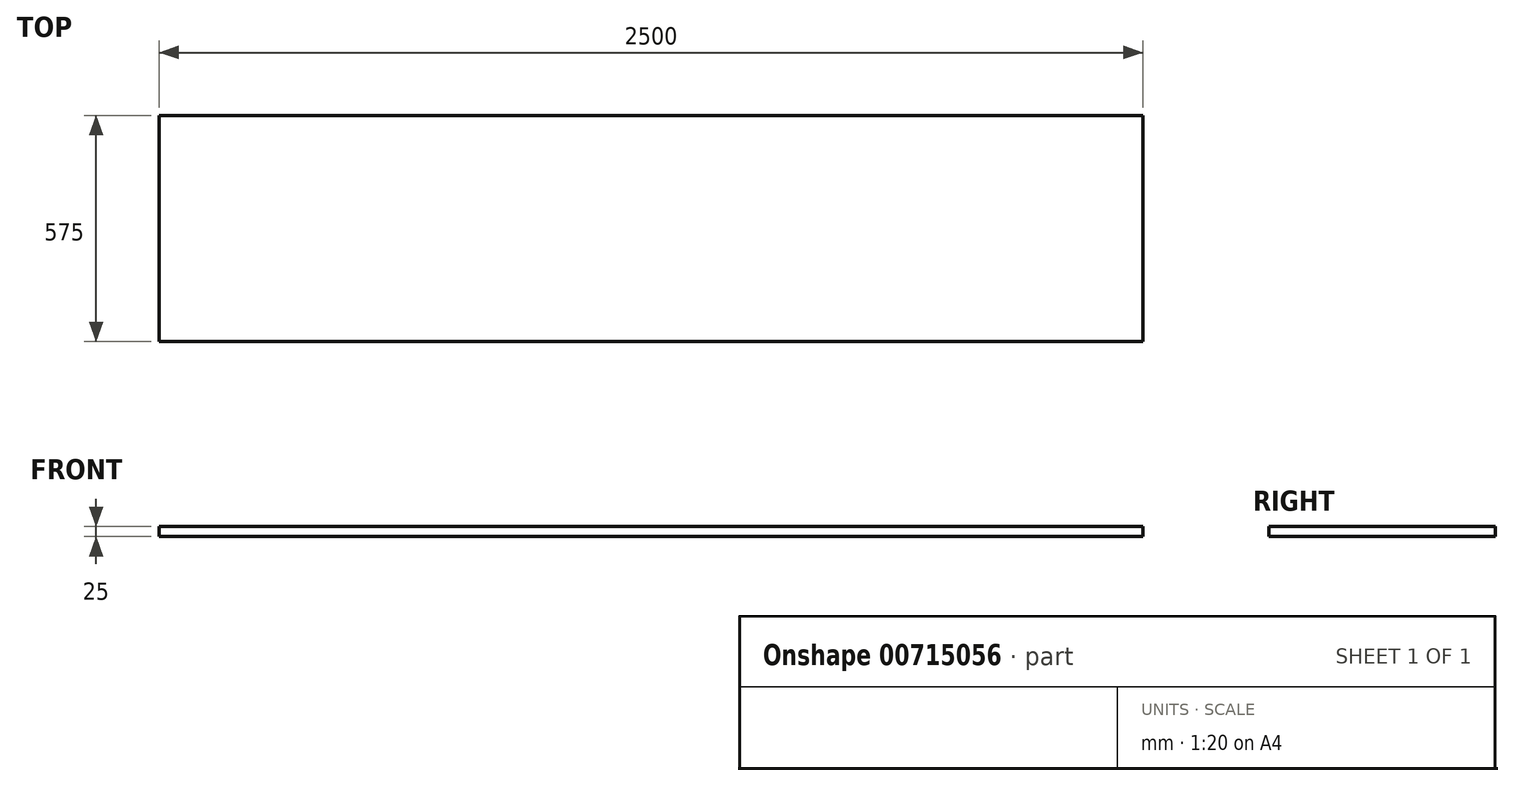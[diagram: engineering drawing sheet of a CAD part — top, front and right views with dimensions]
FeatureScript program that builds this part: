
annotation { "Feature Type Name" : "Feature", "Feature Type Description" : "" }
export const myFeature = defineFeature(function(context is Context, id is Id, definition is map)
    precondition{}
    {
        {
            var Q0;
            Q0=qCreatedBy(makeId("Top.planeOp"),FACE);
            var sketch = newSketch(context, id + "F0", { "sketchPlane" : qUnion([Q0])});
            skLineSegment(sketch, "E0.bottom", {"start": v(1250, 287.5) * mm, "end": v(-1250, 287.5) * mm});
            skLineSegment(sketch, "E0.top", {"start": v(1250, -287.5) * mm, "end": v(-1250, -287.5) * mm});
            skLineSegment(sketch, "E0.left", {"start": v(1250, 287.5) * mm, "end": v(1250, -287.5) * mm});
            skLineSegment(sketch, "E0.right", {"start": v(-1250, 287.5) * mm, "end": v(-1250, -287.5) * mm});
            skPoint(sketch, "E0.middle", {"position": v(0, 0) * mm});
            skSolve(sketch);
        }
        {
            var Q0;
            Q0=makeQuery(id+"F0.imprint","IMPRINT",FACE,{"disambiguationData":[TD([[makeQuery(id+"F0.imprint","IMPRINT",EDGE,{"derivedFrom":sQuery(id+"F0.wireOp",EDGE,"E0.bottom")}),1.0]])]});
            extrude(context, id + "F1", {"entities" : qUnion([Q0]), "depth" : 25 * mm, "offsetDistance" : 25 * mm});
        }
    });
